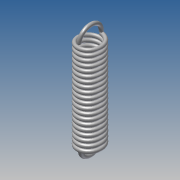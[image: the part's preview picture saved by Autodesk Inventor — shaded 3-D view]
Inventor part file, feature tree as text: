
AUTODESK INVENTOR PART (.ipt)
format: ipt  version: 2014 SP1 (Build 180222100, 222)  size: 1,570,816 bytes
history: native  units: in
note: dims shown in document units (in); Inventor stores cm internally (conversion verified against a paired STEP export)
features: sketch x8, plane x2, revolve x2, extrude x2, helix x1
ambient origin geometry x8: Origin, YZ Plane, XZ Plane, XY Plane, X Axis, Y Axis, Z Axis, Center Point
bodies: Solid1 (feature_tree)
feature tree (15):
  helix  "Coil1"  [1 undecoded]
  sketch  "Sketch11"  dims[d19=180.0deg d20=0.2in]
  plane  "Work Plane1"
  revolve  "Revolution1"  [1 undecoded]
  sketch  "Sketch14"  dims[d24=0.3in d25=0.1in d26=0.0in]
  plane  "Work Plane2"
  extrude  "Extrusion2"  Depth=0.2in
  revolve  "Revolution2"  Angle=180.0deg
  extrude  "Extrusion3"  Depth=0.1in TaperAngle=0.0deg
  sketch  "Sketch1"  dims[d2=0.6in]
  sketch  "Sketch3"  dims[d3=0.25in d4=1.0in d5=7.874in d6=0.0in d7=90.0deg d8=90.0deg d9=0.0in d10=0.0in d18=0.2in]
  sketch  "Sketch12"  dims[d21=0.02in d22=0.0in d23=180.0deg]
  sketch  "Sketch15"
  sketch  "Sketch17"
  sketch  "Sketch18"
note: 2 required parameter values undecoded (feature->parameter linkage not recoverable at this tier; creation-order binding heuristic only, values carry confidence <= 0.55)